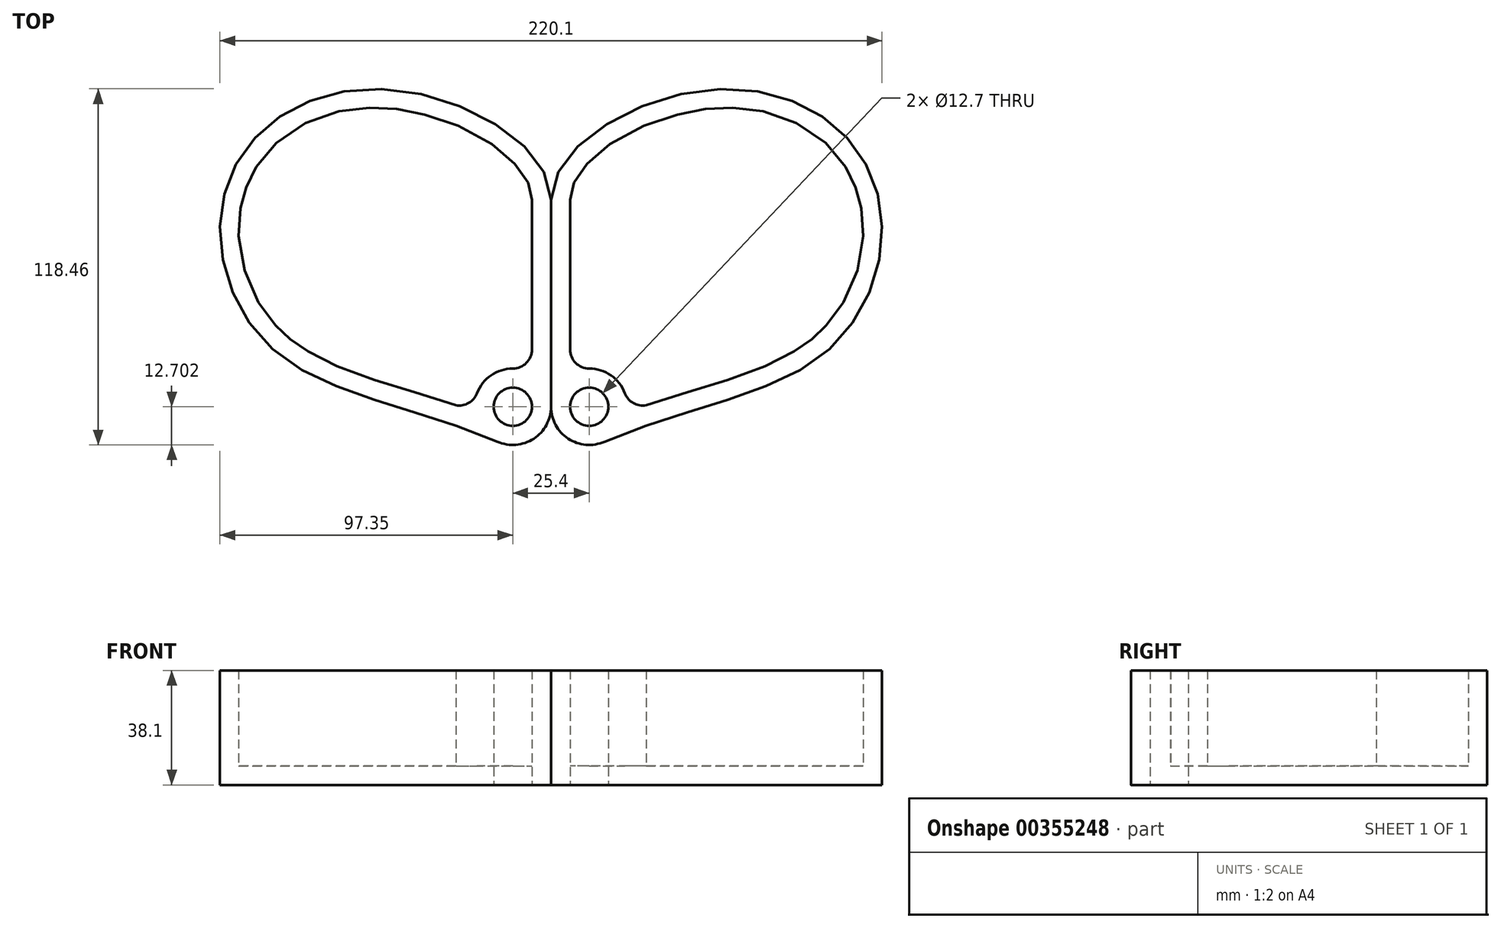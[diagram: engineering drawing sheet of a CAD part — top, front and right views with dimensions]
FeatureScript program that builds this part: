
annotation { "Feature Type Name" : "Feature", "Feature Type Description" : "" }
export const myFeature = defineFeature(function(context is Context, id is Id, definition is map)
    precondition{}
    {
        {
            var Q0;
            Q0=qCreatedBy(makeId("Top.planeOp"),FACE);
            var sketch = newSketch(context, id + "F0", { "sketchPlane" : qUnion([Q0])});
            skLineSegment(sketch, "E0", {"start": v(0, 90.23) * mm, "end": v(0, 21.33) * mm});
            skLineSegment(sketch, "E1", {"start": v(-6.35, 90.23) * mm, "end": v(-6.35, 40.38) * mm});
            skCircle(sketch, "E2", {"center": v(-12.7, 21.33) * mm, "radius": 6.35 * mm});
            skFitSpline(sketch, "E3", {"points": [v(3.59, 5.24) * mm, v(0.25, 7.52) * mm, v(-6.63, 11.6) * mm, v(-17.3, 16.55) * mm, v(-28.13, 20.64) * mm, v(-38.88, 24.13) * mm, v(-49.36, 27.32) * mm, v(-59.36, 30.46) * mm, v(-68.66, 33.78) * mm, v(-75.64, 36.87) * mm, v(-80.67, 39.63) * mm, v(-83.56, 41.5) * mm, v(-85.71, 43.07) * mm, v(-87.25, 44.3) * mm, v(-88.72, 45.58) * mm, v(-90.59, 47.38) * mm, v(-92.76, 49.78) * mm, v(-95.9, 53.9) * mm, v(-99.15, 59.5) * mm, v(-101.91, 66.74) * mm, v(-103.5, 74.23) * mm, v(-103.82, 80.47) * mm, v(-103.46, 85.32) * mm, v(-102.9, 88.87) * mm, v(-102.17, 91.71) * mm, v(-101.43, 93.91) * mm, v(-100.6, 96.06) * mm, v(-99.37, 98.65) * mm, v(-97, 102.61) * mm, v(-93.32, 107.17) * mm, v(-87.86, 111.9) * mm, v(-81.45, 115.78) * mm, v(-74.2, 118.66) * mm, v(-67.58, 120.14) * mm, v(-62, 120.7) * mm, v(-57.67, 120.8) * mm, v(-53.22, 120.54) * mm, v(-48.65, 119.95) * mm, v(-44.02, 119.02) * mm, v(-37.86, 117.38) * mm, v(-30.34, 114.6) * mm, v(-22.11, 110.33) * mm, v(-16.32, 106.2) * mm, v(-12.58, 102.7) * mm, v(-10.25, 100.06) * mm, v(-8.46, 97.43) * mm, v(-7.22, 94.9) * mm, v(-6.5, 92.5) * mm, v(-6.35, 90.99) * mm, v(-6.35, 90.23) * mm]});
            skArc(sketch, "E4", {"start": v(-12.7, 34.03) * mm, "mid": v(-19.92, 31.78) * mm, "end": v(-24.58, 25.82) * mm});
            skPoint(sketch, "E5.visualSharp", {"position": v(-25.27, 19.52) * mm});
            skArc(sketch, "E5.filletArc", {"start": v(-32.52, 22.04) * mm, "mid": v(-27.8, 22.34) * mm, "end": v(-24.58, 25.82) * mm});
            skArc(sketch, "E6.filletArc", {"start": v(-12.7, 34.03) * mm, "mid": v(-8.2, 35.9) * mm, "end": v(-6.35, 40.38) * mm});
            skFitSpline(sketch, "E7", {"points": [v(0, 0) * mm, v(-91.36, 39.48) * mm, v(-107.09, 96.88) * mm, v(-55.18, 127) * mm, v(0, 90.23) * mm], "startDerivative": vector(-298.93, 204.52) * mm, "endDerivative": vector(0, -228.5) * mm});
            skArc(sketch, "E8", {"start": v(-17.8, 9.7) * mm, "mid": v(-5.75, 10.7) * mm, "end": v(0, 21.33) * mm});
            skSolve(sketch);
        }
        {
            var Q0;
            Q0=makeQuery(id+"F0.imprint","IMPRINT",FACE,{"disambiguationData":[TD([[makeQuery(id+"F0.imprint","IMPRINT",EDGE,{"derivedFrom":sQuery(id+"F0.wireOp",EDGE,"E0")}),-1.0]])]});
            extrude(context, id + "F1", {"entities" : qUnion([Q0]), "depth" : 38.1 * mm});
        }
        {
            var Q0;
            Q0=makeQuery(id+"F0.imprint","IMPRINT",FACE,{"disambiguationData":[TD([[makeQuery(id+"F0.imprint","IMPRINT",EDGE,{"derivedFrom":sQuery(id+"F0.wireOp",EDGE,"E1")}),-1.0]])]});
            extrude(context, id + "F2", {"entities" : qUnion([Q0]), "operationType" : NewBodyOperationType.ADD, "depth" : 6.35 * mm});
        }
        {
            var Q0;
            Q0=makeQuery(id+"F1.opExtrude","SWEPT_BODY",BODY,{"disambiguationData":[OSD([sQuery(id+"F0.wireOp",EDGE,"E0"),sQuery(id+"F0.wireOp",EDGE,"E1"),sQuery(id+"F0.wireOp",EDGE,"E2"),sQuery(id+"F0.wireOp",EDGE,"E3"),sQuery(id+"F0.wireOp",EDGE,"E4"),sQuery(id+"F0.wireOp",EDGE,"E5.filletArc"),sQuery(id+"F0.wireOp",EDGE,"E6.filletArc"),sQuery(id+"F0.wireOp",EDGE,"E7"),sQuery(id+"F0.wireOp",EDGE,"E8")])]});
            var Q1;
            Q1=qCreatedBy(makeId("Right.planeOp"),FACE);
            mirror(context, id + "F3", {"entities" : qUnion([Q0]), "mirrorPlane" : qUnion([Q1])});
        }
    });
